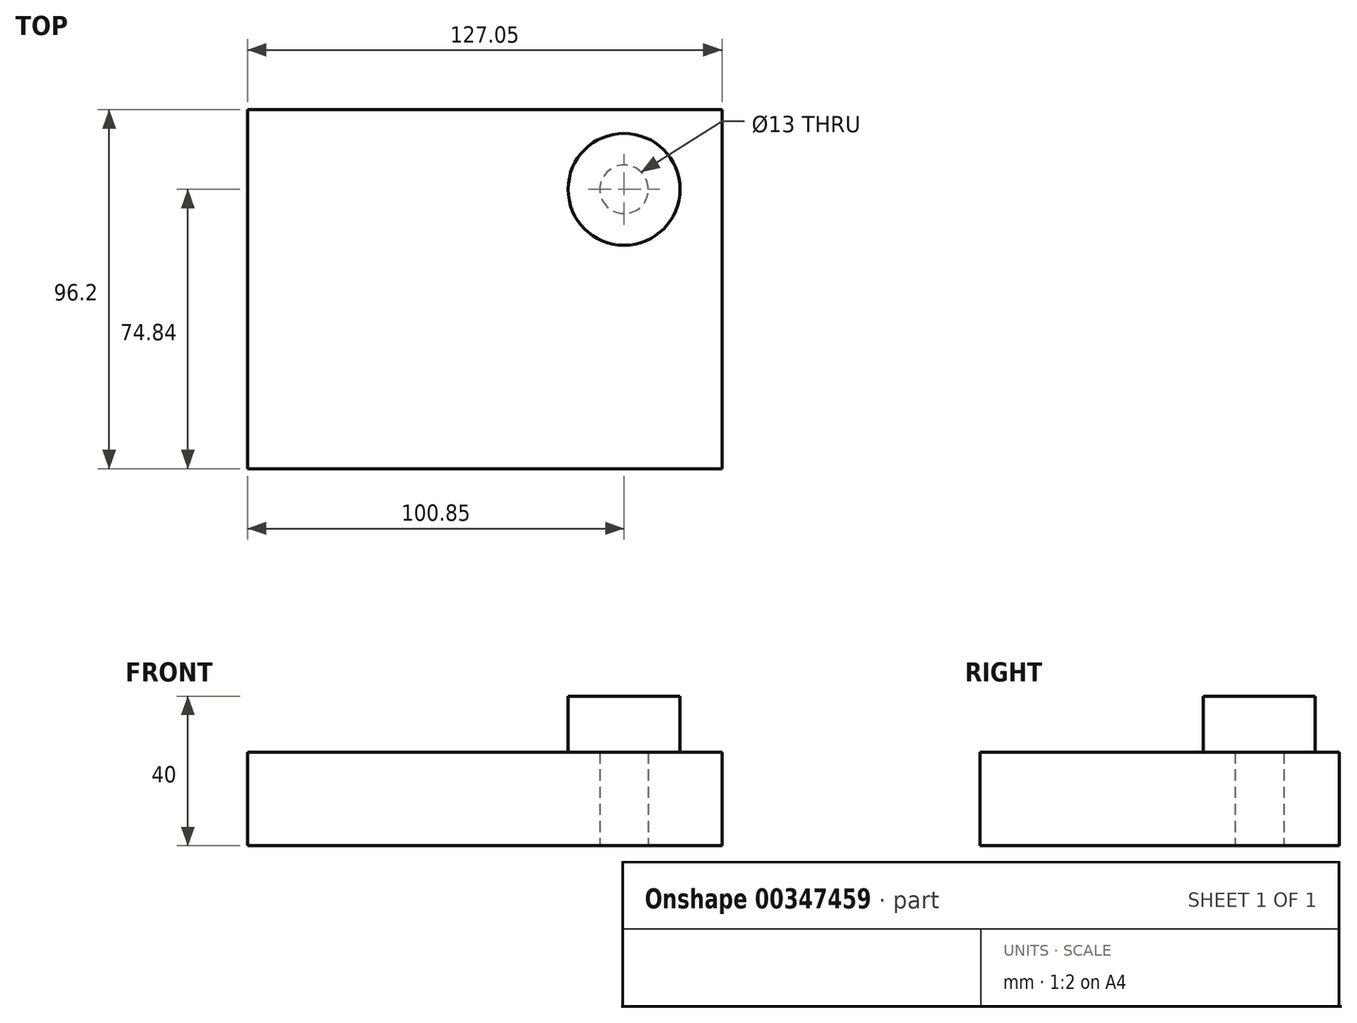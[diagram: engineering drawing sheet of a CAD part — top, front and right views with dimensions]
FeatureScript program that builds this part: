
annotation { "Feature Type Name" : "Feature", "Feature Type Description" : "" }
export const myFeature = defineFeature(function(context is Context, id is Id, definition is map)
    precondition{}
    {
        {
            var Q0;
            Q0=qCreatedBy(makeId("Top.planeOp"),FACE);
            var sketch = newSketch(context, id + "F0", { "sketchPlane" : qUnion([Q0])});
            skLineSegment(sketch, "E0.bottom", {"start": v(-36.04, 63.68) * mm, "end": v(91, 63.68) * mm});
            skLineSegment(sketch, "E0.top", {"start": v(-36.04, -32.52) * mm, "end": v(91, -32.52) * mm});
            skLineSegment(sketch, "E0.left", {"start": v(-36.04, 63.68) * mm, "end": v(-36.04, -32.52) * mm});
            skLineSegment(sketch, "E0.right", {"start": v(91, 63.68) * mm, "end": v(91, -32.52) * mm});
            skCircle(sketch, "E1", {"center": v(64.81, 42.32) * mm, "radius": 6.5 * mm});
            skSolve(sketch);
        }
        {
            var Q0;
            Q0 = qSketchRegion(id + "F0", true);
            extrude(context, id + "F1", {"entities" : qUnion([Q0]), "depth" : 25 * mm});
        }
        {
            var Q0;
            Q0=makeQuery(id+"F1.opExtrude","CAP_FACE",FACE,{"disambiguationData":[OSD([sQuery(id+"F0.wireOp",EDGE,"E0.bottom"),sQuery(id+"F0.wireOp",EDGE,"E0.top"),sQuery(id+"F0.wireOp",EDGE,"E0.left"),sQuery(id+"F0.wireOp",EDGE,"E0.right"),sQuery(id+"F0.wireOp",EDGE,"E1")])],"isStart":false});
            var sketch = newSketch(context, id + "F2", { "sketchPlane" : qUnion([Q0])});
            skCircle(sketch, "E2", {"center": v(64.81, 42.32) * mm, "radius": 15 * mm});
            skSolve(sketch);
        }
        {
            var Q0;
            Q0 = qSketchRegion(id + "F2", true);
            extrude(context, id + "F3", {"entities" : qUnion([Q0]), "depth" : 15 * mm});
        }
        {
            var Q0;
            Q0=makeQuery(id+"F3.opExtrude","CAP_FACE",FACE,{"disambiguationData":[OSD([sQuery(id+"F2.wireOp",EDGE,"E2")])],"isStart":false});
            var sketch = newSketch(context, id + "F4", { "sketchPlane" : qUnion([Q0])});
            skCircle(sketch, "E3", {"center": v(64.81, 42.32) * mm, "radius": 10 * mm});
            skSolve(sketch);
        }
    });
